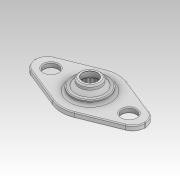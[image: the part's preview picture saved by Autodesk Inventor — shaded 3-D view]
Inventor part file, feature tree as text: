
AUTODESK INVENTOR PART (.ipt)
format: ipt  version: 2020 (Build 240168000, 168)  size: 985,600 bytes
history: native  units: mm
features: sketch x8, other x7, extrude x6, revolve x3, fillet x3, pattern_circular x1, imported_body x1
ambient origin geometry x8: Origin, YZ Plane, XZ Plane, XY Plane, X Axis, Y Axis, Z Axis, Center Point
bodies: Solid1 (feature_tree)
feature tree (29):
  other  "HD_mastersketch.ipt"
  other  "Blocks"
  revolve  "Revolution1"  [1 undecoded]
  extrude  "Extrusion1"  Depth=5.0mm
  extrude  "Extrusion2"  TaperAngle=0.0deg  [1 undecoded]
  fillet  "Fillet1"  [1 undecoded]
  extrude  "Extrusion7"  Depth=12.6mm
  extrude  "Extrusion10"  TaperAngle=0.0deg  [1 undecoded]
  pattern_circular  "Circular Pattern1"  Angle=90.0deg  [1 undecoded]
  revolve  "Revolution3"  [1 undecoded]
  fillet  "Fillet5"  Radius=0.75mm
  fillet  "Fillet6"  Radius=10.9mm
  revolve  "Revolution4"  [1 undecoded]
  extrude  "Extrusion8"  Depth=200.0mm TaperAngle=360.0deg
  extrude  "Extrusion9"  Depth=0.2mm
  other  "608 bearing"
  other  "Belt"
  other  "Rotor"
  imported_body  "Base"
  sketch  "Sketch8"  dims[d1=10.0mm d24=7.0mm d25=22.0mm d26=8.0mm]
  sketch  "Sketch9"  dims[d2=90.0deg d3=5.0mm d4=10.0mm]
  sketch  "Sketch15"  dims[d5=15.0mm d6=0.0mm d7=0.0mm d8=0.0mm d9=0.0mm]
  sketch  "Sketch16"  dims[d10=7.0mm d44=12.6mm]
  sketch  "Sketch17"  dims[d45=10.0mm d46=0.0mm d47=0.0mm d48=0.0mm]
  sketch  "Sketch18"  dims[d49=4.5mm d50=0.0mm]
  sketch  "Sketch19"  dims[d51=8.726646mm]
  sketch  "Sketch20"  dims[d52=1.0mm d53=90.0deg d54=0.5mm d55=0.75mm d56=10.9mm d58=4.5mm d59=0.0mm d60=200.0mm d61=360.0deg d63=0.2mm d68=6.0mm d69=4.1mm d70=4.2mm d72=45.0deg d73=2.0mm d74=0.75mm d75=0.75mm d76=0.1mm d77=0.1mm d78=90.0deg d79=0.8mm d80=45.0deg d81=45.0deg d82=12.6mm]
  other  "608 bearing:1"
  other  "608 bearing:2"
note: 7 required parameter values undecoded (feature->parameter linkage not recoverable at this tier; creation-order binding heuristic only, values carry confidence <= 0.55)